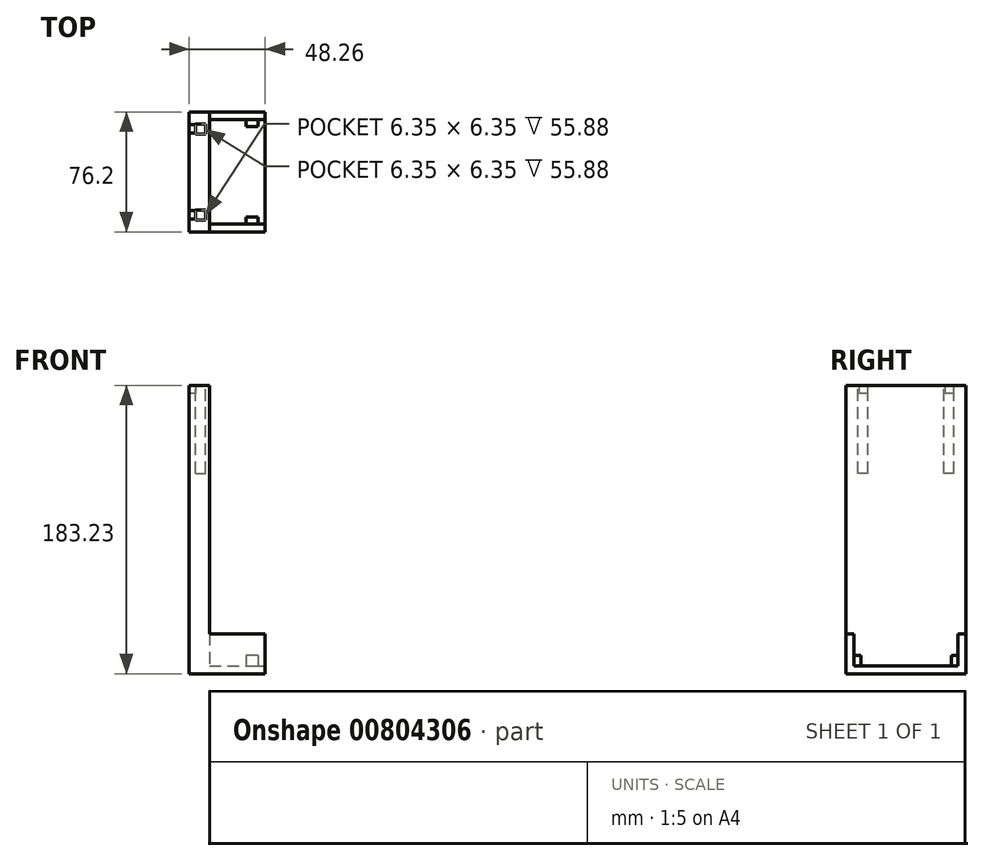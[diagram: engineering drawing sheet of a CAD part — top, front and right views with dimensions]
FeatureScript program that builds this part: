
annotation { "Feature Type Name" : "Feature", "Feature Type Description" : "" }
export const myFeature = defineFeature(function(context is Context, id is Id, definition is map)
    precondition{}
    {
        {
            var Q0;
            Q0=qCreatedBy(makeId("Front.planeOp"),FACE);
            var sketch = newSketch(context, id + "F0", { "sketchPlane" : qUnion([Q0])});
            skLineSegment(sketch, "E0.left", {"start": v(12.7, 0) * mm, "end": v(12.7, 5.42) * mm});
            skLineSegment(sketch, "E1.bottom", {"start": v(12.7, 0) * mm, "end": v(0, 0) * mm});
            skLineSegment(sketch, "E1.top", {"start": v(12.7, 183.23) * mm, "end": v(0, 183.23) * mm});
            skLineSegment(sketch, "E1.left", {"start": v(12.7, 0) * mm, "end": v(12.7, 183.23) * mm});
            skLineSegment(sketch, "E1.right", {"start": v(0, 0) * mm, "end": v(0, 183.23) * mm});
            skLineSegment(sketch, "E2.left", {"start": v(12.7, 5.42) * mm, "end": v(12.7, 23.56) * mm});
            skSolve(sketch);
        }
        {
            var Q0;
            {var subQ0=sQuery(id+"F0.wireOp",EDGE,"5597d51d-3641-4ac6-9092-4d10421c2b9a");Q0=makeQuery(id+"F0.imprint","IMPRINT",FACE,{"disambiguationData":[TD([[makeQuery(id+"F0.imprint","IMPRINT",EDGE,{"derivedFrom":subQ0}),1.0]])]});}
            var Q1;
            {var subQ3=sQuery(id+"F0.wireOp",EDGE,"z3cI9lcN-gAAq-FJT3-k5LZ-xhfdyOAxLoxo.bottom");Q1=makeQuery(id+"F0.imprint","IMPRINT",FACE,{"disambiguationData":[TD([[makeQuery(id+"F0.imprint","IMPRINT",EDGE,{"derivedFrom":subQ3}),1.0]])]});}
            var Q2;
            {var subQ3=sQuery(id+"F0.wireOp",EDGE,"E0.left");Q2=makeQuery(id+"F0.imprint","IMPRINT",FACE,{"disambiguationData":[TD([[makeQuery(id+"F0.imprint","IMPRINT",EDGE,{"derivedFrom":subQ3}),1.0]])]});}
            var Q3;
            {var subQ0=sQuery(id+"F0.wireOp",EDGE,"E0.bottom");Q3=makeQuery(id+"F0.imprint","IMPRINT",FACE,{"disambiguationData":[TD([[makeQuery(id+"F0.imprint","IMPRINT",EDGE,{"derivedFrom":subQ0}),1.0]])]});}
            extrude(context, id + "F1", {"entities" : qUnion([Q0, Q1, Q2, Q3]), "depth" : 76.2 * mm, "offsetDistance" : 25.4 * mm});
        }
        {
            var Q0;
            Q0=qCreatedBy(makeId("Top.planeOp"),FACE);
            var sketch = newSketch(context, id + "F2", { "sketchPlane" : qUnion([Q0])});
            skLineSegment(sketch, "E3.bottom", {"start": v(0, 0) * mm, "end": v(48.26, 0) * mm});
            skLineSegment(sketch, "E3.top", {"start": v(0, -76.2) * mm, "end": v(48.26, -76.2) * mm});
            skLineSegment(sketch, "E3.left", {"start": v(0, 0) * mm, "end": v(0, -76.2) * mm});
            skLineSegment(sketch, "E3.right", {"start": v(48.26, 0) * mm, "end": v(48.26, -76.2) * mm});
            skLineSegment(sketch, "E4.bottom", {"start": v(48.26, -76.2) * mm, "end": v(30.48, -76.2) * mm});
            skLineSegment(sketch, "E4.top", {"start": v(48.26, 0) * mm, "end": v(43.18, 0) * mm});
            skLineSegment(sketch, "E4.left", {"start": v(48.26, -76.2) * mm, "end": v(48.26, 0) * mm});
            skLineSegment(sketch, "E5.top", {"start": v(0, -5.07) * mm, "end": v(48.26, -5.07) * mm});
            skLineSegment(sketch, "E5.left", {"start": v(0, 0) * mm, "end": v(0, -5.07) * mm});
            skLineSegment(sketch, "E5.right", {"start": v(48.26, 0) * mm, "end": v(48.26, -5.07) * mm});
            skLineSegment(sketch, "E6.top", {"start": v(0, -71.18) * mm, "end": v(48.26, -71.18) * mm});
            skLineSegment(sketch, "E6.left", {"start": v(0, -76.2) * mm, "end": v(0, -71.18) * mm});
            skLineSegment(sketch, "E6.right", {"start": v(48.26, -76.2) * mm, "end": v(48.26, -71.18) * mm});
            skLineSegment(sketch, "E7.bottom", {"start": v(27.79, -71.18) * mm, "end": v(35.56, -71.18) * mm});
            skSolve(sketch);
        }
        {
            var Q0;
            {var subQ3=sQuery(id+"F2.wireOp",EDGE,"E6.top");var subQ9=makeQuery(id+"F2.imprint","IMPRINT",VERTEX,{"disambiguationData":[OD(0.0)],"derivedFrom":subQ3});Q0=makeQuery(id+"F2.imprint","IMPRINT",FACE,{"disambiguationData":[TD([[makeQuery(id+"F2.imprint","IMPRINT",EDGE,{"disambiguationData":[TD([[subQ9,1.0]])],"derivedFrom":subQ3}),-1.0]])]});}
            var Q1;
            {var subQ3=sQuery(id+"F2.wireOp",EDGE,"E6.top");var subQ9=makeQuery(id+"F2.imprint","IMPRINT",VERTEX,{"disambiguationData":[OD(0.0)],"derivedFrom":subQ3});Q1=makeQuery(id+"F2.imprint","IMPRINT",FACE,{"disambiguationData":[TD([[makeQuery(id+"F2.imprint","IMPRINT",EDGE,{"disambiguationData":[TD([[subQ9,1.0]])],"derivedFrom":subQ3}),-1.0]])]});}
            var Q2;
            {var subQ5=sQuery(id+"F2.wireOp",EDGE,"E5.top");Q2=makeQuery(id+"F2.imprint","IMPRINT",FACE,{"disambiguationData":[TD([[makeQuery(id+"F2.imprint","IMPRINT",EDGE,{"derivedFrom":subQ5}),1.0]])]});}
            var Q3;
            {var subQ5=sQuery(id+"F2.wireOp",EDGE,"E5.top");Q3=makeQuery(id+"F2.imprint","IMPRINT",FACE,{"disambiguationData":[TD([[makeQuery(id+"F2.imprint","IMPRINT",EDGE,{"derivedFrom":subQ5}),1.0]])]});}
            extrude(context, id + "F3", {"entities" : qUnion([Q0, Q1, Q2, Q3]), "operationType" : NewBodyOperationType.ADD, "depth" : 25.4 * mm, "offsetDistance" : 25.4 * mm});
        }
        {
            var Q0;
            {var subQ0=sQuery(id+"F2.wireOp",EDGE,"E6.top");var subQ5=sQuery(id+"F2.wireOp",EDGE,"E5.top");var subQ6=makeQuery(id+"F2.imprint","IMPRINT",EDGE,{"derivedFrom":subQ5});var subQ11=makeQuery(id+"F2.imprint","IMPRINT",VERTEX,{"disambiguationData":[OD(0.0)],"derivedFrom":subQ0});var subQ13=makeQuery(id+"F2.imprint","IMPRINT",EDGE,{"disambiguationData":[TD([[subQ11,1.0]])],"derivedFrom":subQ0});Q0=qUnion([makeQuery(id+"F2.imprint","IMPRINT",FACE,{"disambiguationData":[TD([[subQ6,1.0]])]}),makeQuery(id+"F2.imprint","IMPRINT",FACE,{"disambiguationData":[TD([[subQ13,-1.0]])]}),makeQuery(id+"F2.imprint","IMPRINT",FACE,{"disambiguationData":[TD([[subQ6,-1.0]])]})]);}
            extrude(context, id + "F4", {"entities" : qUnion([Q0]), "operationType" : NewBodyOperationType.ADD, "depth" : 5.08 * mm, "offsetDistance" : 25.4 * mm});
        }
        {
            var Q0;
            Q0=qCreatedBy(makeId("Top.planeOp"),FACE);
            var sketch = newSketch(context, id + "F5", { "sketchPlane" : qUnion([Q0])});
            skLineSegment(sketch, "E8.top", {"start": v(43.67, -5.07) * mm, "end": v(36.05, -5.07) * mm});
            skLineSegment(sketch, "E9.bottom", {"start": v(43.67, -71.18) * mm, "end": v(36.05, -71.18) * mm});
            skLineSegment(sketch, "E9.top", {"start": v(43.67, -66.8) * mm, "end": v(36.05, -66.8) * mm});
            skLineSegment(sketch, "E9.left", {"start": v(43.67, -71.18) * mm, "end": v(43.67, -66.8) * mm});
            skLineSegment(sketch, "E9.right", {"start": v(36.05, -71.18) * mm, "end": v(36.05, -66.8) * mm});
            skLineSegment(sketch, "E10.top", {"start": v(43.67, -9.45) * mm, "end": v(36.05, -9.45) * mm});
            skLineSegment(sketch, "E10.left", {"start": v(43.67, -5.07) * mm, "end": v(43.67, -9.45) * mm});
            skLineSegment(sketch, "E10.right", {"start": v(36.05, -5.07) * mm, "end": v(36.05, -9.45) * mm});
            skSolve(sketch);
        }
        {
            var Q0;
            Q0 = qSketchRegion(id + "F5", true);
            extrude(context, id + "F6", {"entities" : qUnion([Q0]), "operationType" : NewBodyOperationType.ADD, "depth" : 11.68 * mm, "offsetDistance" : 25.4 * mm});
        }
        {
            var Q0;
            Q0=makeQuery(id+"F1.opExtrude","SWEPT_FACE",FACE,{"disambiguationData":[OSD([sQuery(id+"F0.wireOp",EDGE,"E1.top")])]});
            var sketch = newSketch(context, id + "F7", { "sketchPlane" : qUnion([Q0])});
            skLineSegment(sketch, "E11.bottom", {"start": v(3.81, -7.62) * mm, "end": v(10.16, -7.62) * mm});
            skLineSegment(sketch, "E11.top", {"start": v(3.81, -13.97) * mm, "end": v(10.16, -13.97) * mm});
            skLineSegment(sketch, "E11.left", {"start": v(3.81, -7.62) * mm, "end": v(3.81, -13.97) * mm});
            skLineSegment(sketch, "E11.right", {"start": v(10.16, -7.62) * mm, "end": v(10.16, -13.97) * mm});
            skLineSegment(sketch, "E12.bottom", {"start": v(3.8, -62.23) * mm, "end": v(10.16, -62.23) * mm});
            skLineSegment(sketch, "E12.top", {"start": v(3.81, -68.58) * mm, "end": v(10.16, -68.58) * mm});
            skLineSegment(sketch, "E12.left", {"start": v(3.8, -62.23) * mm, "end": v(3.81, -68.58) * mm});
            skLineSegment(sketch, "E12.right", {"start": v(10.16, -62.23) * mm, "end": v(10.16, -68.58) * mm});
            skSolve(sketch);
        }
        {
            var Q0;
            Q0 = qSketchRegion(id + "F7", true);
            extrude(context, id + "F8", {"entities" : qUnion([Q0]), "operationType" : NewBodyOperationType.REMOVE, "oppositeDirection" : true, "depth" : 55.88 * mm, "offsetDistance" : 25.4 * mm});
        }
        {
            var Q0;
            Q0=qCreatedBy(makeId("Right.planeOp"),FACE);
            var sketch = newSketch(context, id + "F9", { "sketchPlane" : qUnion([Q0])});
            skLineSegment(sketch, "E13.bottom", {"start": v(-62.74, 183.23) * mm, "end": v(-68.07, 183.23) * mm});
            skLineSegment(sketch, "E13.top", {"start": v(-62.74, 177.9) * mm, "end": v(-68.07, 177.9) * mm});
            skLineSegment(sketch, "E13.left", {"start": v(-62.74, 183.23) * mm, "end": v(-62.74, 177.9) * mm});
            skLineSegment(sketch, "E13.right", {"start": v(-68.07, 183.23) * mm, "end": v(-68.07, 177.9) * mm});
            skLineSegment(sketch, "E14.bottom", {"start": v(-8.13, 183.23) * mm, "end": v(-13.46, 183.23) * mm});
            skLineSegment(sketch, "E14.top", {"start": v(-8.13, 177.9) * mm, "end": v(-13.46, 177.9) * mm});
            skLineSegment(sketch, "E14.left", {"start": v(-8.13, 183.23) * mm, "end": v(-8.13, 177.9) * mm});
            skLineSegment(sketch, "E14.right", {"start": v(-13.46, 183.23) * mm, "end": v(-13.46, 177.9) * mm});
            skSolve(sketch);
        }
        {
            var Q0;
            Q0 = qSketchRegion(id + "F9", true);
            extrude(context, id + "F10", {"entities" : qUnion([Q0]), "operationType" : NewBodyOperationType.REMOVE, "depth" : 5.08 * mm, "offsetDistance" : 25.4 * mm});
        }
    });
